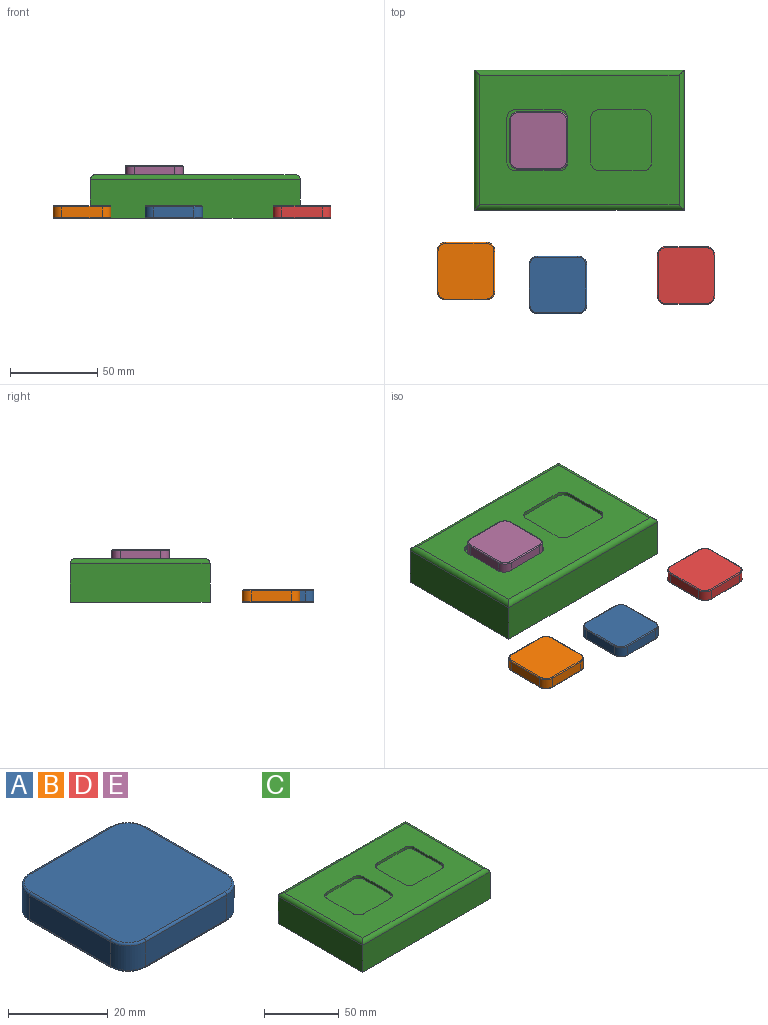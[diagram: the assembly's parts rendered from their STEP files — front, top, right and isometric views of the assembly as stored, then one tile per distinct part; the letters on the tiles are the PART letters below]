
ASSEMBLY  parts=5 mates=4
PART A: 28 faces, bbox 33.8x33.8x7 mm
  f0: plane 23x6mm, normal (1,0,0), area 138mm2, adj f1,f7,f15,f23
  f1: cylinder r=5mm len=6mm, axis (0,0,-1), area 47.1mm2, adj f0,f2,f13,f21
  f2: plane 23x6mm, normal (0,1,0), area 138mm2, adj f1,f3,f12,f20
  f3: cylinder r=5mm len=6mm, axis (0,0,-1), area 47.1mm2, adj f2,f4,f14,f22
  f4: plane 23x6mm, normal (-1,0,0), area 138mm2, adj f3,f5,f16,f24
  f5: cylinder r=5mm len=6mm, axis (0,0,-1), area 47.1mm2, adj f4,f6,f18,f26
  f6: plane 23x6mm, normal (0,-1,0), area 138mm2, adj f5,f7,f19,f27
  f7: cylinder r=5mm len=6mm, axis (0,0,-1), area 47.1mm2, adj f0,f6,f17,f25
  f8: plane 32x32mm, normal (0,0,1), area 1006.6mm2, adj f12,f13,f14,f15,f16,f17,f18,f19
  f9: plane 32x32mm, normal (0,0,-1), area 475.7mm2, adj f10,f20,f21,f22,f23,f24,f25,f26
  f10: cylinder r=13mm len=26mm, axis (0,0,-1), area 163.4mm2, adj f9,f11
  f11: plane 26x26mm, normal (0,0,-1), area 530.9mm2, adj f10
  f12: cylinder r=0.5mm len=23mm, axis (1,0,0), area 18.1mm2, adj f2,f8,f13,f14
  f13: torus R=4.5mm, axis (0,0,1), area 5.9mm2, adj f1,f8,f12,f15
  f14: torus R=4.5mm, axis (0,0,1), area 5.9mm2, adj f3,f8,f12,f16
  f15: cylinder r=0.5mm len=23mm, axis (0,-1,0), area 18.1mm2, adj f0,f8,f13,f17
  f16: cylinder r=0.5mm len=23mm, axis (0,1,0), area 18.1mm2, adj f4,f8,f14,f18
  f17: torus R=4.5mm, axis (0,0,1), area 5.9mm2, adj f7,f8,f15,f19
  f18: torus R=4.5mm, axis (0,0,1), area 5.9mm2, adj f5,f8,f16,f19
  f19: cylinder r=0.5mm len=23mm, axis (-1,0,0), area 18.1mm2, adj f6,f8,f17,f18
  f20: cylinder r=0.5mm len=23mm, axis (-1,0,0), area 18.1mm2, adj f2,f9,f21,f22
  f21: torus R=4.5mm, axis (0,0,1), area 5.9mm2, adj f1,f9,f20,f23
  f22: torus R=4.5mm, axis (0,0,1), area 5.9mm2, adj f3,f9,f20,f24
  f23: cylinder r=0.5mm len=23mm, axis (0,1,0), area 18.1mm2, adj f0,f9,f21,f25
  f24: cylinder r=0.5mm len=23mm, axis (0,-1,0), area 18.1mm2, adj f4,f9,f22,f26
  f25: torus R=4.5mm, axis (0,0,1), area 5.9mm2, adj f7,f9,f23,f27
  f26: torus R=4.5mm, axis (0,0,1), area 5.9mm2, adj f5,f9,f24,f27
  f27: cylinder r=0.5mm len=23mm, axis (1,0,0), area 18.1mm2, adj f6,f9,f25,f26
PART B: same geometry as A
PART C: 28 faces, bbox 120x80x25 mm
  f0: plane 120x22mm, normal (0,-1,0), area 2640mm2, adj f1,f3,f5,f24
  f1: plane 80x22mm, normal (1,0,0), area 1760mm2, adj f0,f2,f5,f25
  f2: plane 120x22mm, normal (0,1,0), area 2640mm2, adj f1,f3,f5,f27
  f3: plane 80x22mm, normal (-1,0,0), area 1760mm2, adj f0,f2,f5,f26
  f4: plane 114x74mm, normal (0,0,1), area 6028.9mm2, adj f6,f7,f8,f9,f10,f11,f12,f13
  f5: plane 120x80mm, normal (0,0,-1), area 9600mm2, adj f0,f1,f2,f3
  f6: plane 25x2mm, normal (-1,0,0), area 50mm2, adj f4,f7,f13,f14
  f7: cylinder r=5mm len=5mm, axis (0,0,1), area 15.7mm2, adj f4,f6,f8,f14
  f8: plane 25x2mm, normal (0,-1,0), area 50mm2, adj f4,f7,f9,f14
  f9: cylinder r=5mm len=5mm, axis (0,0,1), area 15.7mm2, adj f4,f8,f10,f14
  f10: plane 25x2mm, normal (1,0,0), area 50mm2, adj f4,f9,f11,f14
  f11: cylinder r=5mm len=5mm, axis (0,0,1), area 15.7mm2, adj f4,f10,f12,f14
  f12: plane 25x2mm, normal (0,1,0), area 50mm2, adj f4,f11,f13,f14
  f13: cylinder r=5mm len=5mm, axis (0,0,1), area 15.7mm2, adj f4,f6,f12,f14
  f14: plane 35x35mm, normal (0,0,1), area 1203.5mm2, adj f6,f7,f8,f9,f10,f11,f12,f13
  f15: plane 25x2mm, normal (-1,0,0), area 50mm2, adj f4,f16,f22,f23
  f16: cylinder r=5mm len=5mm, axis (0,0,1), area 15.7mm2, adj f4,f15,f17,f23
  f17: plane 25x2mm, normal (0,-1,0), area 50mm2, adj f4,f16,f18,f23
  f18: cylinder r=5mm len=5mm, axis (0,0,1), area 15.7mm2, adj f4,f17,f19,f23
  f19: plane 25x2mm, normal (1,0,0), area 50mm2, adj f4,f18,f20,f23
  f20: cylinder r=5mm len=5mm, axis (0,0,1), area 15.7mm2, adj f4,f19,f21,f23
  f21: plane 25x2mm, normal (0,1,0), area 50mm2, adj f4,f20,f22,f23
  f22: cylinder r=5mm len=5mm, axis (0,0,1), area 15.7mm2, adj f4,f15,f21,f23
  f23: plane 35x35mm, normal (0,0,1), area 1203.5mm2, adj f15,f16,f17,f18,f19,f20,f21,f22
  f24: cylinder r=3mm len=120mm, axis (-1,0,0), area 555.2mm2, adj f0,f4,f25,f26
  f25: cylinder r=3mm len=80mm, axis (0,-1,0), area 366.7mm2, adj f1,f4,f24,f27
  f26: cylinder r=3mm len=80mm, axis (0,1,0), area 366.7mm2, adj f3,f4,f24,f27
  f27: cylinder r=3mm len=120mm, axis (1,0,0), area 555.2mm2, adj f2,f4,f25,f26
PART D: same geometry as A
PART E: same geometry as A
PLACE A t=(-13.99,-82.56,-8.38)mm
PLACE B t=(-66.56,-74.64,-8.38)mm
PLACE C t=(-1.7,0.28,-8.38)mm fixed
PLACE D t=(59.31,-77.18,-8.38)mm
PLACE E t=(-25.14,0.02,14.62)mm
MATE planar A.f10 <-> D.f10  axis (0,0,-1) through (-13.99,-82.56,-6.38)mm
MATE planar B.f7 <-> C.f5  axis (0,0,-1) through (-55.06,-86.14,-8.38)mm
MATE planar E.f1 <-> C.f23  axis (0,0,-1) through (-13.64,11.52,14.62)mm
MATE planar B.f10 <-> A.f10  axis (0,0,-1) through (-66.56,-74.64,-6.38)mm
